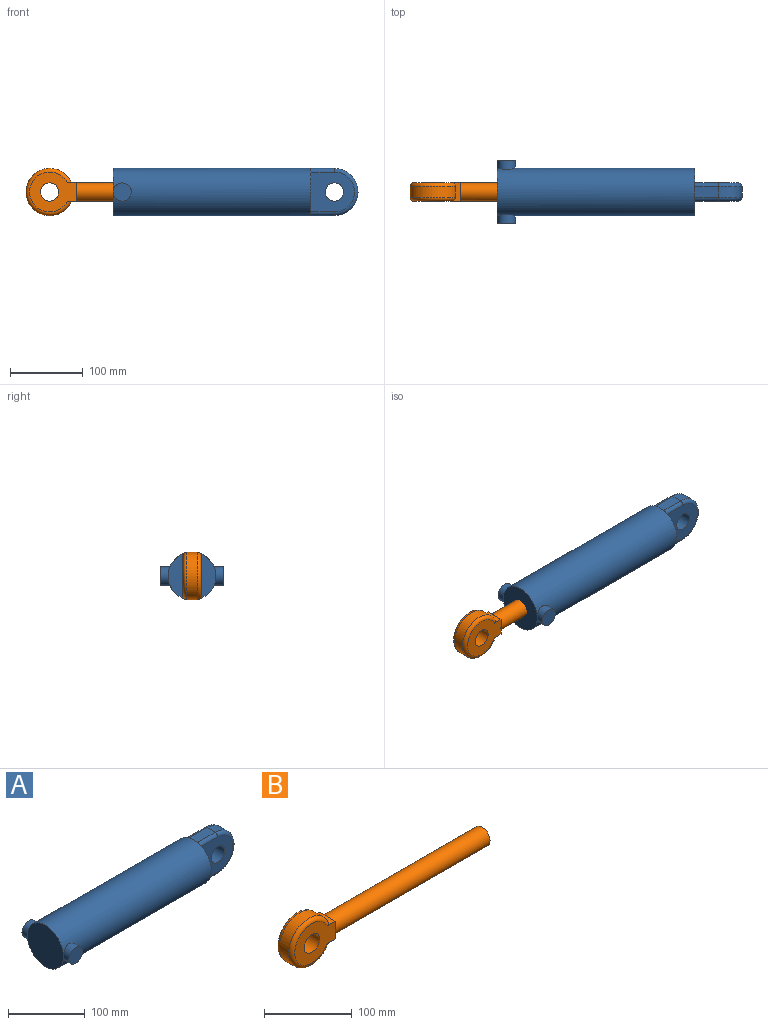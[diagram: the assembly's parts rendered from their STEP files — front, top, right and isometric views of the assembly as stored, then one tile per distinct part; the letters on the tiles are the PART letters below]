
ASSEMBLY  parts=2 mates=1
PART A: 26 faces, bbox 339.7x86x70.4 mm
  f0: cylinder r=33mm len=272mm, axis (1,0,0), area 55399mm2, adj f1,f2,f3,f8,f11,f12,f13,f14
  f1: plane 5.21x1.36mm, normal (-1,0,0), area 1.7mm2, adj f0,f6,f16
  f2: plane 5.21x1.36mm, normal (-1,0,0), area 1.7mm2, adj f0,f4,f18
  f3: plane 5.21x1.36mm, normal (-1,0,0), area 1.7mm2, adj f0,f4,f21
  f4: plane 32.5x15mm, normal (0,0,-1), area 487.5mm2, adj f2,f3,f5,f12,f18,f21
  f5: cylinder r=32.5mm len=65mm, axis (0,1,0), area 1531.5mm2, adj f4,f6,f17,f20
  f6: plane 32.5x15mm, normal (0,0,1), area 487.5mm2, adj f1,f5,f8,f13,f16,f19
  f7: cylinder r=12.5mm len=25mm, axis (0,1,0), area 1963.5mm2, adj f9,f10
  f8: plane 5.21x1.36mm, normal (-1,0,0), area 1.7mm2, adj f0,f6,f19
  f9: plane 60x55mm, normal (0,-1,0), area 2484.5mm2, adj f7,f15,f19,f20,f21
  f10: plane 60x55mm, normal (0,1,0), area 2484.5mm2, adj f7,f11,f16,f17,f18
  f11: plane 62.27x22.07mm, normal (1,0,0), area 908.4mm2, adj f0,f10,f16,f18
  f12: plane 11.45x0.5mm, normal (1,0,0), area 3.8mm2, adj f0,f4
  f13: plane 11.45x0.5mm, normal (1,0,0), area 3.8mm2, adj f0,f6
  f14: plane 66x66mm, normal (-1,0,0), area 3421.2mm2, adj f0
  f15: plane 62.27x22.07mm, normal (1,0,0), area 908.4mm2, adj f0,f9,f19,f21
  f16: cylinder r=5mm len=32.5mm, axis (-1,0,0), area 255.3mm2, adj f1,f6,f10,f11,f17
  f17: torus R=27.5mm, axis (0,-1,0), area 757.1mm2, adj f5,f10,f16,f18
  f18: cylinder r=5mm len=32.5mm, axis (1,0,0), area 255.3mm2, adj f2,f4,f10,f11,f17
  f19: cylinder r=5mm len=32.5mm, axis (1,0,0), area 255.3mm2, adj f6,f8,f9,f15,f20
  f20: torus R=27.5mm, axis (0,-1,0), area 757.1mm2, adj f5,f9,f19,f21
  f21: cylinder r=5mm len=32.5mm, axis (-1,0,0), area 255.3mm2, adj f3,f4,f9,f15,f20
  f22: plane 25x25mm, normal (0,-1,0), area 490.9mm2, adj f23
  f23: cylinder r=12.5mm len=25mm, axis (0,1,0), area 881.3mm2, adj f0,f22
  f24: cylinder r=12.5mm len=25mm, axis (0,1,0), area 880.9mm2, adj f0,f25
  f25: plane 25x25mm, normal (0,1,0), area 490.9mm2, adj f24
PART B: 14 faces, bbox 322.7x25x70.4 mm
  f0: plane 12.5x12.5mm, normal (1,0,0), area 33.5mm2, adj f5,f9,f12
  f1: plane 12.5x12.5mm, normal (1,0,0), area 33.5mm2, adj f3,f9,f12
  f2: plane 12.5x12.5mm, normal (1,0,0), area 33.5mm2, adj f3,f8,f12
  f3: plane 25x13.01mm, normal (0,0,1), area 199.2mm2, adj f1,f2,f4,f8,f9,f10,f11
  f4: cylinder r=32.5mm len=65mm, axis (0,1,0), area 2678.1mm2, adj f3,f5,f10,f11
  f5: plane 25x13.01mm, normal (0,0,-1), area 199.2mm2, adj f0,f4,f7,f8,f9,f10,f11
  f6: cylinder r=12.5mm len=25mm, axis (0,1,0), area 1963.5mm2, adj f8,f9
  f7: plane 12.5x12.5mm, normal (1,0,0), area 33.5mm2, adj f5,f8,f12
  f8: plane 65x55mm, normal (0,-1,0), area 2159.4mm2, adj f2,f3,f5,f6,f7,f11
  f9: plane 65x55mm, normal (0,1,0), area 2159.4mm2, adj f0,f1,f3,f5,f6,f10
  f10: torus R=27.5mm, axis (0,-1,0), area 1311.9mm2, adj f3,f4,f5,f9
  f11: torus R=27.5mm, axis (0,-1,0), area 1311.9mm2, adj f3,f4,f5,f8
  f12: cylinder r=12.5mm len=250mm, axis (-1,0,0), area 19635mm2, adj f0,f1,f2,f7,f13
  f13: plane 25x25mm, normal (1,0,0), area 490.9mm2, adj f12
PLACE A t=(200,-12.3,20.82)mm fixed
PLACE B t=(200,-12.3,20.82)mm
MATE slider A.f0 <-> B.f12  axis (1,0,0) through (198.2,-24.8,30.36)mm
